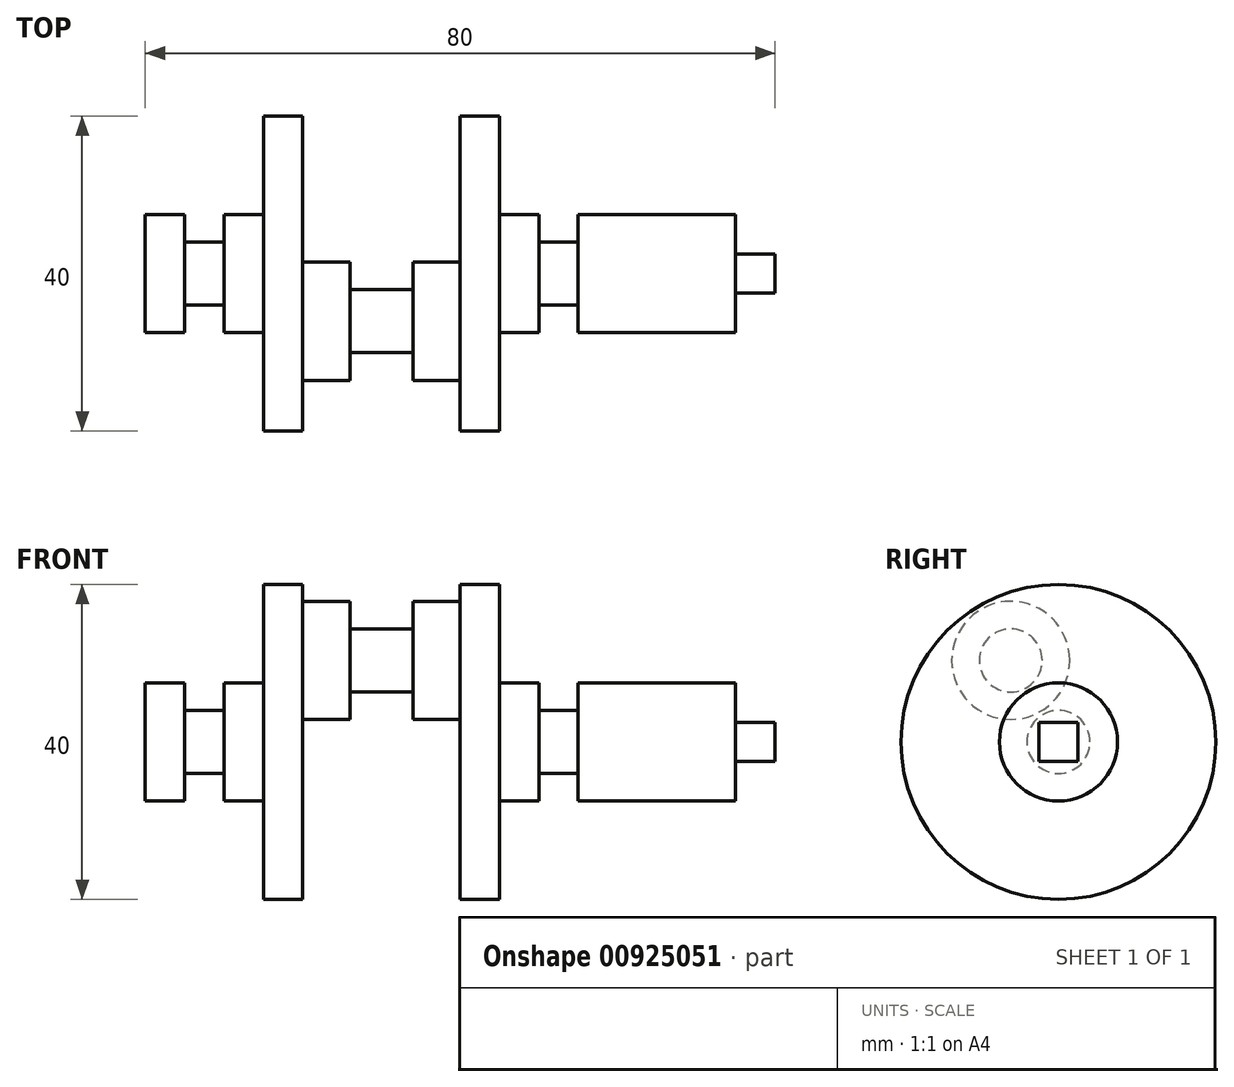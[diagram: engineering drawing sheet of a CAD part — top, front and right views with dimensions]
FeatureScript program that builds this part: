
annotation { "Feature Type Name" : "Feature", "Feature Type Description" : "" }
export const myFeature = defineFeature(function(context is Context, id is Id, definition is map)
    precondition{}
    {
        {
            var Q0;
            Q0=qCreatedBy(makeId("Right.planeOp"),FACE);
            var sketch = newSketch(context, id + "F0", { "sketchPlane" : qUnion([Q0])});
            skCircle(sketch, "E0", {"center": v(17.25, 0) * mm, "radius": 20 * mm});
            skSolve(sketch);
        }
        {
            var Q0;
            Q0=makeQuery(id+"F0.imprint","IMPRINT",FACE,{"disambiguationData":[TD([[makeQuery(id+"F0.imprint","IMPRINT",EDGE,{"derivedFrom":sQuery(id+"F0.wireOp",EDGE,"E0")}),1.0]])]});
            extrude(context, id + "F1", {"entities" : qUnion([Q0]), "depth" : 5 * mm, "offsetDistance" : 25 * mm});
        }
        {
            var Q0;
            Q0=makeQuery(id+"F1.opExtrude","CAP_FACE",FACE,{"disambiguationData":[OSD([sQuery(id+"F0.wireOp",EDGE,"E0")])],"isStart":false});
            var sketch = newSketch(context, id + "F2", { "sketchPlane" : qUnion([Q0])});
            skCircle(sketch, "E1", {"center": v(11.2, 10.36) * mm, "radius": 7.5 * mm});
            skSolve(sketch);
        }
        {
            var Q0;
            Q0=makeQuery(id+"F1.opExtrude","CAP_FACE",FACE,{"disambiguationData":[OSD([sQuery(id+"F0.wireOp",EDGE,"E0")])],"isStart":true});
            var sketch = newSketch(context, id + "F3", { "sketchPlane" : qUnion([Q0])});
            skCircle(sketch, "E2", {"center": v(-17.25, 0) * mm, "radius": 7.5 * mm});
            skSolve(sketch);
        }
        {
            var Q0;
            Q0=makeQuery(id+"F3.imprint","IMPRINT",FACE,{"disambiguationData":[TD([[makeQuery(id+"F3.imprint","IMPRINT",EDGE,{"derivedFrom":sQuery(id+"F3.wireOp",EDGE,"E2")}),1.0]])]});
            extrude(context, id + "F4", {"entities" : qUnion([Q0]), "operationType" : NewBodyOperationType.ADD, "depth" : 5 * mm, "offsetDistance" : 25 * mm});
        }
        {
            var Q0;
            Q0=makeQuery(id+"F4.opExtrude","CAP_FACE",FACE,{"disambiguationData":[OSD([sQuery(id+"F3.wireOp",EDGE,"E2")])],"isStart":false});
            var sketch = newSketch(context, id + "F5", { "sketchPlane" : qUnion([Q0])});
            skCircle(sketch, "E3", {"center": v(-17.25, 0) * mm, "radius": 4 * mm});
            skSolve(sketch);
        }
        {
            var Q0;
            Q0=makeQuery(id+"F5.imprint","IMPRINT",FACE,{"disambiguationData":[TD([[makeQuery(id+"F5.imprint","IMPRINT",EDGE,{"derivedFrom":sQuery(id+"F5.wireOp",EDGE,"E3")}),1.0]])]});
            extrude(context, id + "F6", {"entities" : qUnion([Q0]), "operationType" : NewBodyOperationType.ADD, "depth" : 5 * mm, "offsetDistance" : 25 * mm});
        }
        {
            var Q0;
            Q0=makeQuery(id+"F6.opExtrude","CAP_FACE",FACE,{"disambiguationData":[OSD([sQuery(id+"F5.wireOp",EDGE,"E3")])],"isStart":false});
            var sketch = newSketch(context, id + "F7", { "sketchPlane" : qUnion([Q0])});
            skCircle(sketch, "E4", {"center": v(-17.25, 0) * mm, "radius": 7.5 * mm});
            skSolve(sketch);
        }
        {
            var Q0;
            Q0=makeQuery(id+"F7.imprint","IMPRINT",FACE,{"disambiguationData":[TD([[makeQuery(id+"F7.imprint","IMPRINT",EDGE,{"derivedFrom":makeQuery(id+"F6.opExtrude","CAP_EDGE",EDGE,{"disambiguationData":[OSD([sQuery(id+"F5.wireOp",EDGE,"E3")])],"isStart":false})}),1.0]])]});
            var Q1;
            Q1=makeQuery(id+"F7.imprint","IMPRINT",FACE,{"disambiguationData":[TD([[makeQuery(id+"F7.imprint","IMPRINT",EDGE,{"derivedFrom":sQuery(id+"F7.wireOp",EDGE,"E4")}),1.0]])]});
            extrude(context, id + "F8", {"entities" : qUnion([Q0, Q1]), "operationType" : NewBodyOperationType.ADD, "depth" : 5 * mm, "offsetDistance" : 25 * mm});
        }
        {
            var Q0;
            Q0=makeQuery(id+"F2.imprint","IMPRINT",FACE,{"disambiguationData":[TD([[makeQuery(id+"F2.imprint","IMPRINT",EDGE,{"derivedFrom":sQuery(id+"F2.wireOp",EDGE,"E1")}),1.0]])]});
            extrude(context, id + "F9", {"entities" : qUnion([Q0]), "operationType" : NewBodyOperationType.ADD, "depth" : 6 * mm, "offsetDistance" : 25 * mm});
        }
        {
            var Q0;
            Q0=makeQuery(id+"F9.opExtrude","CAP_FACE",FACE,{"disambiguationData":[OSD([sQuery(id+"F2.wireOp",EDGE,"E1")])],"isStart":false});
            var sketch = newSketch(context, id + "F10", { "sketchPlane" : qUnion([Q0])});
            skCircle(sketch, "E5", {"center": v(11.2, 10.36) * mm, "radius": 4 * mm});
            skSolve(sketch);
        }
        {
            var Q0;
            Q0=makeQuery(id+"F10.imprint","IMPRINT",FACE,{"disambiguationData":[TD([[makeQuery(id+"F10.imprint","IMPRINT",EDGE,{"derivedFrom":sQuery(id+"F10.wireOp",EDGE,"E5")}),1.0]])]});
            extrude(context, id + "F11", {"entities" : qUnion([Q0]), "operationType" : NewBodyOperationType.ADD, "depth" : 4 * mm, "offsetDistance" : 25 * mm});
        }
        {
            var Q0;
            Q0=makeQuery(id+"F1.opExtrude","SWEPT_BODY",BODY,{"disambiguationData":[OSD([sQuery(id+"F0.wireOp",EDGE,"E0")])]});
            var Q1;
            Q1=makeQuery(id+"F11.opExtrude","CAP_FACE",FACE,{"disambiguationData":[OSD([sQuery(id+"F10.wireOp",EDGE,"E5")])],"isStart":false});
            mirror(context, id + "F12", {"operationType" : NewBodyOperationType.ADD, "entities" : qUnion([Q0]), "mirrorPlane" : qUnion([Q1])});
        }
        {
            var Q0;
            Q0=makeQuery(id+"F12.opPattern","COPY",FACE,{"derivedFrom":makeQuery(id+"F8.opExtrude","CAP_FACE",FACE,{"disambiguationData":[OSD([sQuery(id+"F7.wireOp",EDGE,"E4")])],"isStart":false}),"instanceName":"1"});
            var sketch = newSketch(context, id + "F13", { "sketchPlane" : qUnion([Q0])});
            skCircle(sketch, "E6", {"center": v(17.25, 0) * mm, "radius": 7.5 * mm});
            skSolve(sketch);
        }
        {
            var Q0;
            Q0=makeQuery(id+"F13.imprint","IMPRINT",FACE,{"disambiguationData":[TD([[makeQuery(id+"F13.imprint","IMPRINT",EDGE,{"derivedFrom":sQuery(id+"F13.wireOp",EDGE,"E6")}),-1.0]])]});
            extrude(context, id + "F14", {"entities" : qUnion([Q0]), "operationType" : NewBodyOperationType.ADD, "depth" : 15 * mm, "offsetDistance" : 25 * mm});
        }
        {
            var Q0;
            Q0=makeQuery(id+"F14.opExtrude","CAP_FACE",FACE,{"disambiguationData":[OSD([sQuery(id+"F13.wireOp",EDGE,"E6")])],"isStart":false});
            var sketch = newSketch(context, id + "F15", { "sketchPlane" : qUnion([Q0])});
            skLineSegment(sketch, "E7.bottom", {"start": v(14.75, 2.5) * mm, "end": v(19.75, 2.5) * mm});
            skLineSegment(sketch, "E7.top", {"start": v(14.75, -2.5) * mm, "end": v(19.75, -2.5) * mm});
            skLineSegment(sketch, "E7.left", {"start": v(14.75, 2.5) * mm, "end": v(14.75, -2.5) * mm});
            skLineSegment(sketch, "E7.right", {"start": v(19.75, 2.5) * mm, "end": v(19.75, -2.5) * mm});
            skSolve(sketch);
        }
        {
            var Q0;
            Q0=makeQuery(id+"F15.imprint","IMPRINT",FACE,{"disambiguationData":[TD([[makeQuery(id+"F15.imprint","IMPRINT",EDGE,{"derivedFrom":sQuery(id+"F15.wireOp",EDGE,"E7.bottom")}),-1.0]])]});
            extrude(context, id + "F16", {"entities" : qUnion([Q0]), "operationType" : NewBodyOperationType.ADD, "depth" : 5 * mm, "offsetDistance" : 25 * mm});
        }
    });
